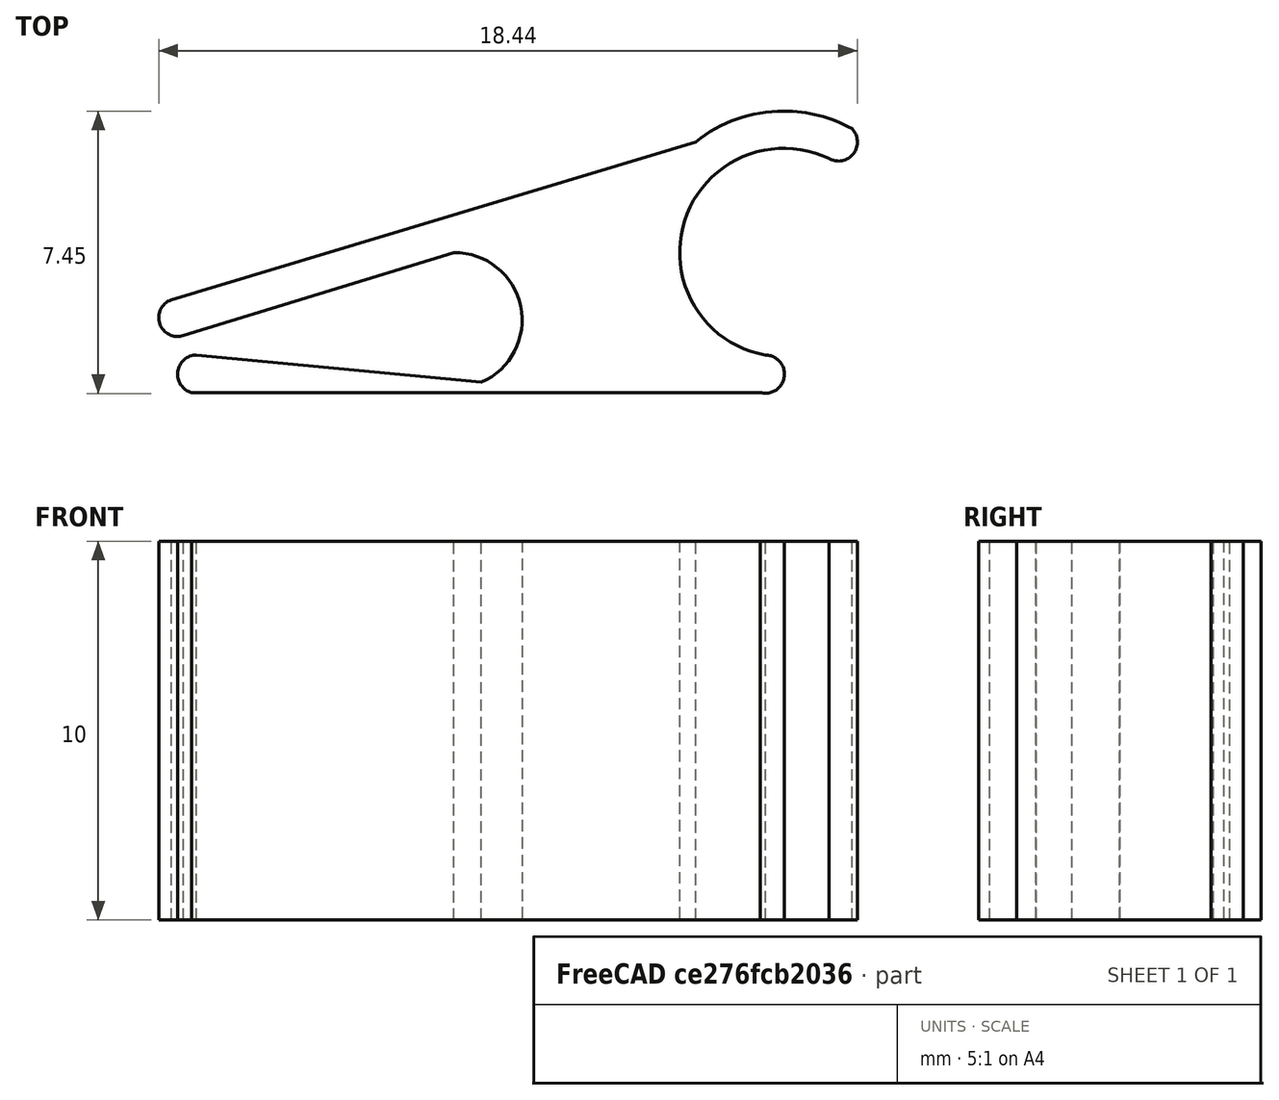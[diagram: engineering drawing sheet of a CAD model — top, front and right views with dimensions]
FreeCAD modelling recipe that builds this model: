
FCSTD DOCUMENT  (FreeCAD 0.18R4 (GitTag))
Label: mask_clips
License: All rights reserved
LicenseURL: http://en.wikipedia.org/wiki/All_rights_reserved
objects: Sketcher::SketchObject×1, PartDesign::Pad×1, PartDesign::Body×1
note: 4 computed .brp shape members not serialized (recipe doc carries the construction recipe); baked Part::Feature solids carry a one-line shape summary decoded from their .brp

FEATURE [Sketcher::SketchObject] Sketch
  MapMode = 5
  Support = -> [XY_Plane]
  sketch-geometry (12):
    g0: ArcOfCircle CenterX=0 CenterY=0 CenterZ=0 NormalX=0 NormalY=0 NormalZ=1 AngleXU=0 Radius=2.75 StartAngle=1.07891 EndAngle=4.53446
    g1: ArcOfCircle CenterX=-0.487337 CenterY=-3.21083 CenterZ=0 NormalX=0 NormalY=0 NormalZ=1 AngleXU=0 Radius=0.504242 StartAngle=4.45157 EndAngle=7.85276
    g2: ArcOfCircle CenterX=1.46694 CenterY=2.90113 CenterZ=0 NormalX=0 NormalY=0 NormalZ=1 AngleXU=0 Radius=0.505915 StartAngle=4.37357 EndAngle=7.20904
    g3: ArcOfCircle CenterX=0 CenterY=0 CenterZ=0 NormalX=0 NormalY=0 NormalZ=1 AngleXU=0 Radius=3.75 StartAngle=1.07891 EndAngle=1.5708
    g4: LineSegment StartX=-0.617366 StartY=-3.69801 StartZ=0 EndX=-15.6294 EndY=-3.69801 EndZ=0
    g5: ArcOfCircle CenterX=0 CenterY=0 CenterZ=0 NormalX=0 NormalY=0 NormalZ=1 AngleXU=0 Radius=3.75 StartAngle=1.5708 EndAngle=1.5708
    g6: LineSegment StartX=-6.8734e-12 StartY=3.75 StartZ=0 EndX=-16.1729 EndY=-1.24852 EndZ=0
    g7: ArcOfCircle CenterX=-16 CenterY=-1.71775 CenterZ=0 NormalX=0 NormalY=0 NormalZ=1 AngleXU=0 Radius=0.500083 StartAngle=1.9239 EndAngle=5.02904
    g8: ArcOfCircle CenterX=-15.5 CenterY=-3.21065 CenterZ=0 NormalX=0 NormalY=0 NormalZ=1 AngleXU=0 Radius=0.504236 StartAngle=1.5708 EndAngle=4.45296
    g9: ArcOfCircle CenterX=-6.5 CenterY=-1.17741 CenterZ=0 NormalX=0 NormalY=0 NormalZ=1 AngleXU=0 Radius=1.33231 StartAngle=4.49271 EndAngle=8.34099
    g10: LineSegment StartX=-15.5 StartY=-2.70642 StartZ=0 EndX=-6.79033 EndY=-2.4777 EndZ=0
    g11: LineSegment StartX=-15.8443 StartY=-2.19297 StartZ=0 EndX=-7.1235 EndY=4e-16 EndZ=0
  constraints (24):
    c: Coincident(g0,g-1)
    c: Distance(g0,g0) = 2.75
    c: Coincident(g1,g0)
    c: Distance(g1,g0) = 1
    c: Coincident(g2,g0)
    c: Distance(g2,g0) = 1
    c: Coincident(g3,g0)
    c: Coincident(g3,g2)
    c: PointOnObject(g3,g-2)
    c: Coincident(g4,g1)
    c: Horizontal(g4)
    c: Coincident(g5,g0)
    c: Coincident(g5,g3)
    c: Coincident(g6,g5)
    c: Coincident(g7,g6)
    c: Coincident(g8,g4)
    c: PointOnObject(g9,g-1)
    c: Coincident(g10,g8)
    c: Coincident(g10,g9)
    c: Coincident(g11,g7)
    c: Coincident(g11,g9)
    c: Distance(g7,g6) = 1
    c: Distance(g8,g4) = 1
    c: Distance(g9,g9) = 2.5
FEATURE [PartDesign::Pad] Pad
  Length = 10
  Length2 = 100
  Profile = -> Sketch
  Type = 0
FEATURE [PartDesign::Body] Body
  Group = -> [Sketch,Pad]
  Origin = -> Origin
  Tip = -> Pad
